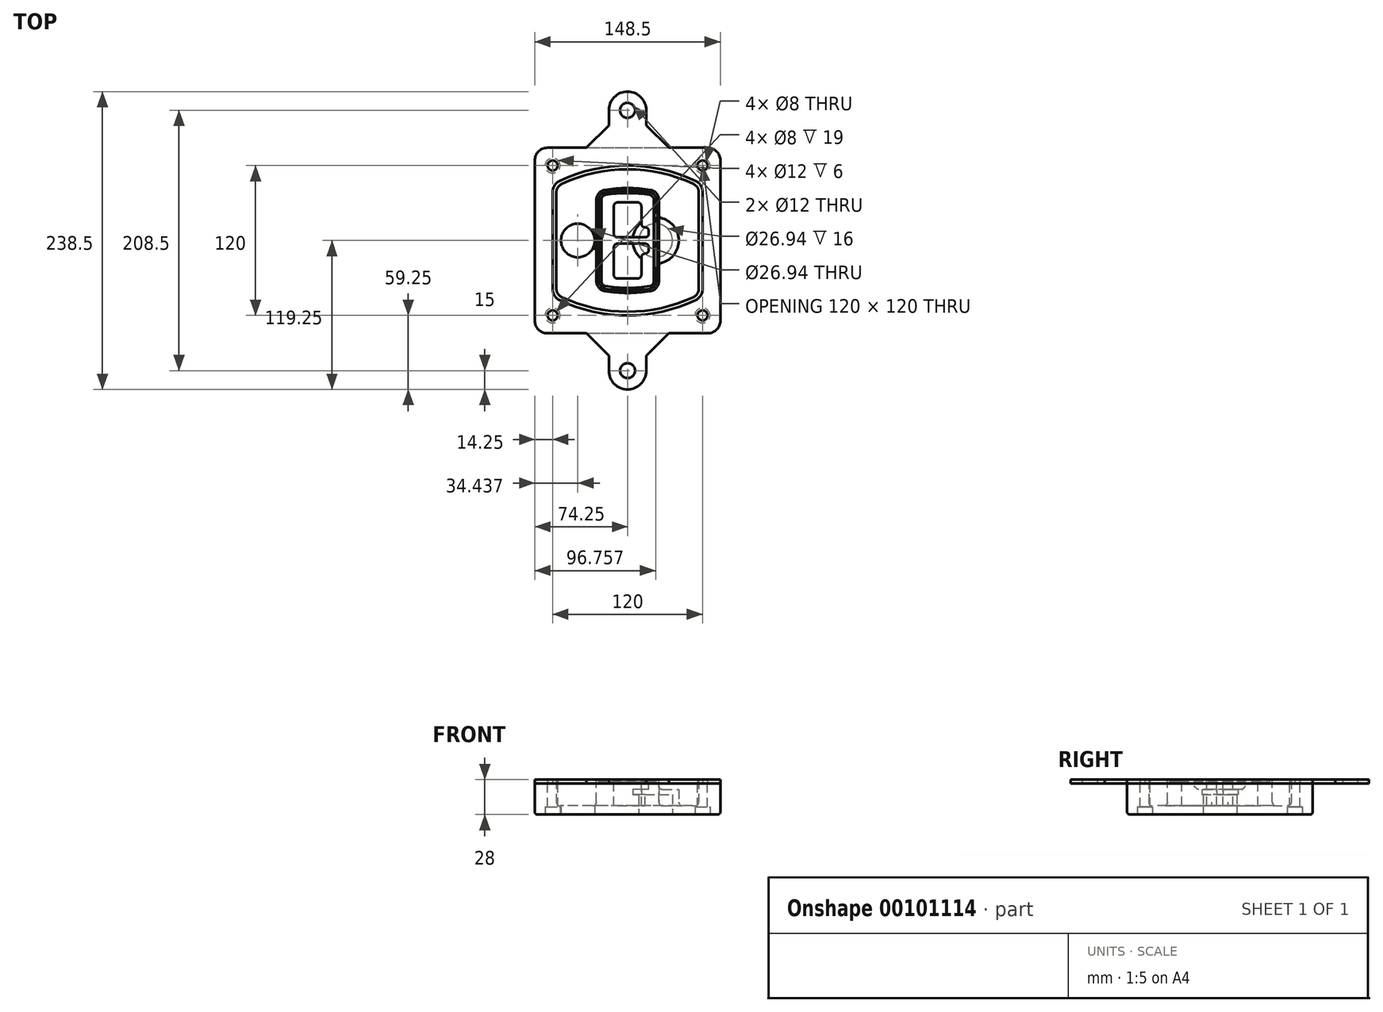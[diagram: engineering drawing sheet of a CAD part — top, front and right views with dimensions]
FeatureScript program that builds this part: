
annotation { "Feature Type Name" : "Feature", "Feature Type Description" : "" }
export const myFeature = defineFeature(function(context is Context, id is Id, definition is map)
    precondition{}
    {
        {
            var Q0;
            Q0=qCreatedBy(makeId("Top.planeOp"),FACE);
            var sketch = newSketch(context, id + "F0", { "sketchPlane" : qUnion([Q0])});
            skPoint(sketch, "E0.rect.middle", {"position": v(0, 0) * mm});
            skLineSegment(sketch, "E1.bottom", {"start": v(-64.25, -74.25) * mm, "end": v(64.25, -74.25) * mm});
            skLineSegment(sketch, "E1.top", {"start": v(-64.25, 74.25) * mm, "end": v(64.25, 74.25) * mm});
            skLineSegment(sketch, "E1.left", {"start": v(-74.25, -64.25) * mm, "end": v(-74.25, 64.25) * mm});
            skLineSegment(sketch, "E1.right", {"start": v(74.25, -64.25) * mm, "end": v(74.25, 64.25) * mm});
            skLineSegment(sketch, "E2", {"start": v(-74.25, 74.25) * mm, "end": v(74.25, -74.25) * mm, "construction": true});
            skLineSegment(sketch, "E3", {"start": v(74.25, 74.25) * mm, "end": v(-74.25, -74.25) * mm, "construction": true});
            skCircle(sketch, "E4", {"center": v(-60, 60) * mm, "radius": 4 * mm});
            skCircle(sketch, "E5", {"center": v(60, 60) * mm, "radius": 4 * mm});
            skCircle(sketch, "E6", {"center": v(60, -60) * mm, "radius": 4 * mm});
            skCircle(sketch, "E7", {"center": v(-60, -60) * mm, "radius": 4 * mm});
            skLineSegment(sketch, "E8", {"start": v(-60, 60) * mm, "end": v(60, 60) * mm, "construction": true});
            skLineSegment(sketch, "E9", {"start": v(60, 60) * mm, "end": v(60, -60) * mm, "construction": true});
            skLineSegment(sketch, "E10", {"start": v(60, -60) * mm, "end": v(-60, -60) * mm, "construction": true});
            skLineSegment(sketch, "E11", {"start": v(-60, -60) * mm, "end": v(-60, 60) * mm, "construction": true});
            skLineSegment(sketch, "E12", {"start": v(-60, 38.83) * mm, "end": v(-60, -38.83) * mm});
            skLineSegment(sketch, "E13", {"start": v(60, 38.83) * mm, "end": v(60, -38.83) * mm});
            skArc(sketch, "E14", {"start": v(54.26, 47.88) * mm, "mid": v(0, 60) * mm, "end": v(-54.26, 47.88) * mm});
            skArc(sketch, "E15", {"start": v(-54.26, -47.88) * mm, "mid": v(0, -60) * mm, "end": v(54.26, -47.88) * mm});
            skLineSegment(sketch, "E16", {"start": v(-60, 0) * mm, "end": v(60, 0) * mm, "construction": true});
            skPoint(sketch, "E17.visualSharp", {"position": v(-60, -45) * mm});
            skArc(sketch, "E17.filletArc", {"start": v(-60, -38.83) * mm, "mid": v(-58.44, -44.2) * mm, "end": v(-54.26, -47.88) * mm});
            skPoint(sketch, "E18.visualSharp", {"position": v(-60, 45) * mm});
            skArc(sketch, "E18.filletArc", {"start": v(-54.26, 47.88) * mm, "mid": v(-58.44, 44.2) * mm, "end": v(-60, 38.83) * mm});
            skPoint(sketch, "E19.visualSharp", {"position": v(60, 45) * mm});
            skArc(sketch, "E19.filletArc", {"start": v(60, 38.83) * mm, "mid": v(58.44, 44.2) * mm, "end": v(54.26, 47.88) * mm});
            skPoint(sketch, "E20.visualSharp", {"position": v(60, -45) * mm});
            skArc(sketch, "E20.filletArc", {"start": v(54.26, -47.88) * mm, "mid": v(58.44, -44.2) * mm, "end": v(60, -38.83) * mm});
            skPoint(sketch, "E21.visualSharp", {"position": v(-74.25, 74.25) * mm});
            skArc(sketch, "E21.filletArc", {"start": v(-64.25, 74.25) * mm, "mid": v(-71.32, 71.32) * mm, "end": v(-74.25, 64.25) * mm});
            skPoint(sketch, "E22.visualSharp", {"position": v(74.25, 74.25) * mm});
            skArc(sketch, "E22.filletArc", {"start": v(74.25, 64.25) * mm, "mid": v(71.32, 71.32) * mm, "end": v(64.25, 74.25) * mm});
            skPoint(sketch, "E23.visualSharp", {"position": v(74.25, -74.25) * mm});
            skArc(sketch, "E23.filletArc", {"start": v(64.25, -74.25) * mm, "mid": v(71.32, -71.32) * mm, "end": v(74.25, -64.25) * mm});
            skPoint(sketch, "E24.visualSharp", {"position": v(-74.25, -74.25) * mm});
            skArc(sketch, "E24.filletArc", {"start": v(-74.25, -64.25) * mm, "mid": v(-71.32, -71.32) * mm, "end": v(-64.25, -74.25) * mm});
            skArc(sketch, "E25.0", {"start": v(57, 38.83) * mm, "mid": v(55.9, 42.58) * mm, "end": v(52.98, 45.17) * mm});
            skLineSegment(sketch, "E25.1", {"start": v(57, 38.83) * mm, "end": v(57, -38.83) * mm});
            skArc(sketch, "E25.2", {"start": v(52.98, -45.17) * mm, "mid": v(55.9, -42.58) * mm, "end": v(57, -38.83) * mm});
            skArc(sketch, "E25.3", {"start": v(-52.98, -45.17) * mm, "mid": v(0, -57) * mm, "end": v(52.98, -45.17) * mm});
            skArc(sketch, "E25.4", {"start": v(-57, -38.83) * mm, "mid": v(-55.9, -42.58) * mm, "end": v(-52.98, -45.17) * mm});
            skArc(sketch, "E25.5", {"start": v(52.98, 45.17) * mm, "mid": v(0, 57) * mm, "end": v(-52.98, 45.17) * mm});
            skLineSegment(sketch, "E25.6", {"start": v(-57, 38.83) * mm, "end": v(-57, -38.83) * mm});
            skArc(sketch, "E25.7", {"start": v(-52.98, 45.17) * mm, "mid": v(-55.9, 42.58) * mm, "end": v(-57, 38.83) * mm});
            skArc(sketch, "E26.0", {"start": v(-55.96, 51.5) * mm, "mid": v(-61.82, 46.33) * mm, "end": v(-64, 38.83) * mm});
            skArc(sketch, "E26.1", {"start": v(55.96, 51.5) * mm, "mid": v(0, 64) * mm, "end": v(-55.96, 51.5) * mm});
            skArc(sketch, "E26.2", {"start": v(64, 38.83) * mm, "mid": v(61.82, 46.33) * mm, "end": v(55.96, 51.5) * mm});
            skLineSegment(sketch, "E26.3", {"start": v(64, 38.83) * mm, "end": v(64, -38.83) * mm});
            skArc(sketch, "E26.4", {"start": v(55.96, -51.5) * mm, "mid": v(61.82, -46.33) * mm, "end": v(64, -38.83) * mm});
            skLineSegment(sketch, "E26.5", {"start": v(-64, 38.83) * mm, "end": v(-64, -38.83) * mm});
            skArc(sketch, "E26.6", {"start": v(-55.96, -51.5) * mm, "mid": v(0, -64) * mm, "end": v(55.96, -51.5) * mm});
            skArc(sketch, "E26.7", {"start": v(-64, -38.83) * mm, "mid": v(-61.82, -46.33) * mm, "end": v(-55.96, -51.5) * mm});
            skSolve(sketch);
        }
        {
            var Q0;
            Q0=makeQuery(id+"F0.imprint","IMPRINT",FACE,{"disambiguationData":[TD([[makeQuery(id+"F0.imprint","IMPRINT",EDGE,{"derivedFrom":sQuery(id+"F0.wireOp",EDGE,"E1.bottom")}),1.0]])]});
            var Q1;
            Q1=makeQuery(id+"F0.imprint","IMPRINT",FACE,{"disambiguationData":[TD([[makeQuery(id+"F0.imprint","IMPRINT",EDGE,{"derivedFrom":sQuery(id+"F0.wireOp",EDGE,"E12")}),1.0]])]});
            var Q2;
            Q2=makeQuery(id+"F0.imprint","IMPRINT",FACE,{"disambiguationData":[TD([[makeQuery(id+"F0.imprint","IMPRINT",EDGE,{"derivedFrom":sQuery(id+"F0.wireOp",EDGE,"E25.0")}),1.0]])]});
            var Q3;
            Q3=makeQuery(id+"F0.imprint","IMPRINT",FACE,{"disambiguationData":[TD([[makeQuery(id+"F0.imprint","IMPRINT",EDGE,{"derivedFrom":sQuery(id+"F0.wireOp",EDGE,"E12")}),-1.0]])]});
            extrude(context, id + "F1", {"entities" : qUnion([Q0, Q1, Q2, Q3]), "oppositeDirection" : true, "depth" : 25 * mm});
        }
        {
            var Q0;
            Q0=makeQuery(id+"F0.imprint","IMPRINT",FACE,{"disambiguationData":[TD([[makeQuery(id+"F0.imprint","IMPRINT",EDGE,{"derivedFrom":sQuery(id+"F0.wireOp",EDGE,"E12")}),1.0]])]});
            extrude(context, id + "F2", {"entities" : qUnion([Q0]), "operationType" : NewBodyOperationType.ADD, "depth" : 3 * mm});
        }
        {
            var Q0;
            Q0=makeQuery(id+"F0.imprint","IMPRINT",FACE,{"disambiguationData":[TD([[makeQuery(id+"F0.imprint","IMPRINT",EDGE,{"derivedFrom":sQuery(id+"F0.wireOp",EDGE,"E25.0")}),1.0]])]});
            extrude(context, id + "F3", {"entities" : qUnion([Q0]), "operationType" : NewBodyOperationType.REMOVE, "oppositeDirection" : true, "depth" : 18 * mm});
        }
        {
            var Q0;
            Q0=makeQuery(id+"F2.opExtrude","CAP_FACE",FACE,{"disambiguationData":[OSD([sQuery(id+"F0.wireOp",EDGE,"E12"),sQuery(id+"F0.wireOp",EDGE,"E13"),sQuery(id+"F0.wireOp",EDGE,"E14"),sQuery(id+"F0.wireOp",EDGE,"E15"),sQuery(id+"F0.wireOp",EDGE,"E17.filletArc"),sQuery(id+"F0.wireOp",EDGE,"E18.filletArc"),sQuery(id+"F0.wireOp",EDGE,"E19.filletArc"),sQuery(id+"F0.wireOp",EDGE,"E20.filletArc"),sQuery(id+"F0.wireOp",EDGE,"E25.0"),sQuery(id+"F0.wireOp",EDGE,"E25.1"),sQuery(id+"F0.wireOp",EDGE,"E25.2"),sQuery(id+"F0.wireOp",EDGE,"E25.3"),sQuery(id+"F0.wireOp",EDGE,"E25.4"),sQuery(id+"F0.wireOp",EDGE,"E25.5"),sQuery(id+"F0.wireOp",EDGE,"E25.6"),sQuery(id+"F0.wireOp",EDGE,"E25.7")])],"isStart":false});
            var sketch = newSketch(context, id + "F4", { "sketchPlane" : qUnion([Q0])});
            skArc(sketch, "E27.0", {"start": v(-18.34, -40.45) * mm, "mid": v(0, -42) * mm, "end": v(18.34, -40.45) * mm});
            skArc(sketch, "E28.0", {"start": v(18.34, 40.45) * mm, "mid": v(0, 42) * mm, "end": v(-18.34, 40.45) * mm});
            skLineSegment(sketch, "E29", {"start": v(-25, 32.57) * mm, "end": v(-25, -32.57) * mm});
            skLineSegment(sketch, "E30", {"start": v(25, 32.57) * mm, "end": v(25, -32.57) * mm});
            skLineSegment(sketch, "E31", {"start": v(-25, 39.1) * mm, "end": v(25, 39.1) * mm, "construction": true});
            skLineSegment(sketch, "E32", {"start": v(-25, -39.1) * mm, "end": v(25, -39.1) * mm, "construction": true});
            skPoint(sketch, "E33.visualSharp", {"position": v(-25, 39.1) * mm});
            skArc(sketch, "E33.filletArc", {"start": v(-18.34, 40.45) * mm, "mid": v(-23.11, 37.73) * mm, "end": v(-25, 32.57) * mm});
            skPoint(sketch, "E34.visualSharp", {"position": v(25, 39.1) * mm});
            skArc(sketch, "E34.filletArc", {"start": v(25, 32.57) * mm, "mid": v(23.11, 37.73) * mm, "end": v(18.34, 40.45) * mm});
            skPoint(sketch, "E35.visualSharp", {"position": v(25, -39.1) * mm});
            skArc(sketch, "E35.filletArc", {"start": v(18.34, -40.45) * mm, "mid": v(23.11, -37.73) * mm, "end": v(25, -32.57) * mm});
            skPoint(sketch, "E36.visualSharp", {"position": v(-25, -39.1) * mm});
            skArc(sketch, "E36.filletArc", {"start": v(-25, -32.57) * mm, "mid": v(-23.11, -37.73) * mm, "end": v(-18.34, -40.45) * mm});
            skArc(sketch, "E37.0", {"start": v(52.98, 45.17) * mm, "mid": v(0, 57) * mm, "end": v(-52.98, 45.17) * mm});
            skArc(sketch, "E37.1", {"start": v(-52.98, 45.17) * mm, "mid": v(-55.9, 42.58) * mm, "end": v(-57, 38.83) * mm});
            skLineSegment(sketch, "E37.2", {"start": v(-57, 38.83) * mm, "end": v(-57, -38.83) * mm});
            skArc(sketch, "E37.3", {"start": v(-57, -38.83) * mm, "mid": v(-55.9, -42.58) * mm, "end": v(-52.98, -45.17) * mm});
            skArc(sketch, "E37.4", {"start": v(-52.98, -45.17) * mm, "mid": v(0, -57) * mm, "end": v(52.98, -45.17) * mm});
            skArc(sketch, "E37.5", {"start": v(52.98, -45.17) * mm, "mid": v(55.9, -42.58) * mm, "end": v(57, -38.83) * mm});
            skLineSegment(sketch, "E37.6", {"start": v(57, 38.83) * mm, "end": v(57, -38.83) * mm});
            skArc(sketch, "E37.7", {"start": v(57, 38.83) * mm, "mid": v(55.9, 42.58) * mm, "end": v(52.98, 45.17) * mm});
            skLineSegment(sketch, "E38.0", {"start": v(23, 32.57) * mm, "end": v(23, -32.57) * mm});
            skArc(sketch, "E38.1", {"start": v(18, -38.48) * mm, "mid": v(21.58, -36.44) * mm, "end": v(23, -32.57) * mm});
            skArc(sketch, "E38.2", {"start": v(-18, -38.48) * mm, "mid": v(0, -40) * mm, "end": v(18, -38.48) * mm});
            skArc(sketch, "E38.3", {"start": v(-23, -32.57) * mm, "mid": v(-21.58, -36.44) * mm, "end": v(-18, -38.48) * mm});
            skLineSegment(sketch, "E38.4", {"start": v(-23, 32.57) * mm, "end": v(-23, -32.57) * mm});
            skArc(sketch, "E38.5", {"start": v(23, 32.57) * mm, "mid": v(21.58, 36.44) * mm, "end": v(18, 38.48) * mm});
            skArc(sketch, "E38.6", {"start": v(-18, 38.48) * mm, "mid": v(-21.58, 36.44) * mm, "end": v(-23, 32.57) * mm});
            skArc(sketch, "E38.7", {"start": v(18, 38.48) * mm, "mid": v(0, 40) * mm, "end": v(-18, 38.48) * mm});
            skArc(sketch, "E39.0", {"start": v(21, 32.57) * mm, "mid": v(20.06, 35.15) * mm, "end": v(17.67, 36.5) * mm});
            skLineSegment(sketch, "E39.1", {"start": v(21, 32.57) * mm, "end": v(21, -32.57) * mm});
            skArc(sketch, "E39.2", {"start": v(17.67, -36.5) * mm, "mid": v(20.06, -35.15) * mm, "end": v(21, -32.57) * mm});
            skArc(sketch, "E39.3", {"start": v(-17.67, -36.5) * mm, "mid": v(0, -38) * mm, "end": v(17.67, -36.5) * mm});
            skArc(sketch, "E39.4", {"start": v(-21, -32.57) * mm, "mid": v(-20.06, -35.15) * mm, "end": v(-17.67, -36.5) * mm});
            skArc(sketch, "E39.5", {"start": v(17.67, 36.5) * mm, "mid": v(0, 38) * mm, "end": v(-17.67, 36.5) * mm});
            skLineSegment(sketch, "E39.6", {"start": v(-21, 32.57) * mm, "end": v(-21, -32.57) * mm});
            skArc(sketch, "E39.7", {"start": v(-17.67, 36.5) * mm, "mid": v(-20.06, 35.15) * mm, "end": v(-21, 32.57) * mm});
            skLineSegment(sketch, "E40", {"start": v(-25, 0) * mm, "end": v(25, 0) * mm, "construction": true});
            skLineSegment(sketch, "E41", {"start": v(-11, 5.5) * mm, "end": v(-11, 27.5) * mm});
            skLineSegment(sketch, "E42", {"start": v(-8, 30.5) * mm, "end": v(8, 30.5) * mm});
            skLineSegment(sketch, "E43", {"start": v(11, 27.5) * mm, "end": v(11, 13.5) * mm});
            skLineSegment(sketch, "E44", {"start": v(14, 10.5) * mm, "end": v(14, 10.5) * mm});
            skLineSegment(sketch, "E45", {"start": v(17, 7.5) * mm, "end": v(17, 5.5) * mm});
            skLineSegment(sketch, "E46", {"start": v(14, 2.5) * mm, "end": v(-8, 2.5) * mm});
            skPoint(sketch, "E47.visualSharp", {"position": v(-11, 30.5) * mm});
            skArc(sketch, "E47.filletArc", {"start": v(-8, 30.5) * mm, "mid": v(-10.12, 29.62) * mm, "end": v(-11, 27.5) * mm});
            skPoint(sketch, "E48.visualSharp", {"position": v(11, 30.5) * mm});
            skArc(sketch, "E48.filletArc", {"start": v(11, 27.5) * mm, "mid": v(10.12, 29.62) * mm, "end": v(8, 30.5) * mm});
            skPoint(sketch, "E49.visualSharp", {"position": v(11, 10.5) * mm});
            skArc(sketch, "E49.filletArc", {"start": v(11, 13.5) * mm, "mid": v(11.88, 11.38) * mm, "end": v(14, 10.5) * mm});
            skPoint(sketch, "E50.visualSharp", {"position": v(17, 10.5) * mm});
            skArc(sketch, "E50.filletArc", {"start": v(17, 7.5) * mm, "mid": v(16.12, 9.62) * mm, "end": v(14, 10.5) * mm});
            skPoint(sketch, "E51.visualSharp", {"position": v(17, 2.5) * mm});
            skArc(sketch, "E51.filletArc", {"start": v(14, 2.5) * mm, "mid": v(16.12, 3.38) * mm, "end": v(17, 5.5) * mm});
            skPoint(sketch, "E52.visualSharp", {"position": v(-11, 2.5) * mm});
            skArc(sketch, "E52.filletArc", {"start": v(-11, 5.5) * mm, "mid": v(-10.12, 3.38) * mm, "end": v(-8, 2.5) * mm});
            skLineSegment(sketch, "E53.0.MirrorCS", {"start": v(14, -2.5) * mm, "end": v(-8, -2.5) * mm});
            skArc(sketch, "E54.0.MirrorCS", {"start": v(-11, -5.5) * mm, "mid": v(-10.12, -3.38) * mm, "end": v(-8, -2.5) * mm});
            skLineSegment(sketch, "E55.0.MirrorCS", {"start": v(-11, -5.5) * mm, "end": v(-11, -27.5) * mm});
            skArc(sketch, "E56.0.MirrorCS", {"start": v(-8, -30.5) * mm, "mid": v(-10.12, -29.62) * mm, "end": v(-11, -27.5) * mm});
            skLineSegment(sketch, "E57.0.MirrorCS", {"start": v(-8, -30.5) * mm, "end": v(8, -30.5) * mm});
            skArc(sketch, "E58.0.MirrorCS", {"start": v(11, -27.5) * mm, "mid": v(10.12, -29.62) * mm, "end": v(8, -30.5) * mm});
            skLineSegment(sketch, "E59.0.MirrorCS", {"start": v(11, -27.5) * mm, "end": v(11, -13.5) * mm});
            skArc(sketch, "E60.0.MirrorCS", {"start": v(11, -13.5) * mm, "mid": v(11.88, -11.38) * mm, "end": v(14, -10.5) * mm});
            skArc(sketch, "E61.0.MirrorCS", {"start": v(17, -7.5) * mm, "mid": v(16.12, -9.62) * mm, "end": v(14, -10.5) * mm});
            skLineSegment(sketch, "E62.0.MirrorCS", {"start": v(17, -7.5) * mm, "end": v(17, -5.5) * mm});
            skArc(sketch, "E63.0.MirrorCS", {"start": v(14, -2.5) * mm, "mid": v(16.12, -3.38) * mm, "end": v(17, -5.5) * mm});
            skSolve(sketch);
        }
        {
            var Q0;
            Q0=makeQuery(id+"F4.imprint","IMPRINT",FACE,{"disambiguationData":[TD([[makeQuery(id+"F4.imprint","IMPRINT",EDGE,{"derivedFrom":sQuery(id+"F4.wireOp",EDGE,"E27.0")}),1.0]])]});
            var Q1;
            Q1=makeQuery(id+"F4.imprint","IMPRINT",FACE,{"disambiguationData":[TD([[makeQuery(id+"F4.imprint","IMPRINT",EDGE,{"derivedFrom":sQuery(id+"F4.wireOp",EDGE,"E38.0")}),-1.0]])]});
            var Q2;
            Q2=makeQuery(id+"F4.imprint","IMPRINT",FACE,{"disambiguationData":[TD([[makeQuery(id+"F4.imprint","IMPRINT",EDGE,{"derivedFrom":sQuery(id+"F4.wireOp",EDGE,"E39.0")}),1.0]])]});
            extrude(context, id + "F5", {"entities" : qUnion([Q0, Q1, Q2]), "operationType" : NewBodyOperationType.ADD, "endBound" : BoundingType.UP_TO_NEXT, "oppositeDirection" : true, "depth" : 25 * mm});
        }
        {
            var Q0;
            Q0=makeQuery(id+"F4.imprint","IMPRINT",FACE,{"disambiguationData":[TD([[makeQuery(id+"F4.imprint","IMPRINT",EDGE,{"derivedFrom":sQuery(id+"F4.wireOp",EDGE,"E38.0")}),-1.0]])]});
            extrude(context, id + "F6", {"entities" : qUnion([Q0]), "operationType" : NewBodyOperationType.REMOVE, "oppositeDirection" : true, "depth" : 2 * mm});
        }
        {
            var Q0;
            Q0=makeQuery(id+"F1.opExtrude","CAP_FACE",FACE,{"disambiguationData":[OSD([sQuery(id+"F0.wireOp",EDGE,"E1.bottom"),sQuery(id+"F0.wireOp",EDGE,"E1.top"),sQuery(id+"F0.wireOp",EDGE,"E1.left"),sQuery(id+"F0.wireOp",EDGE,"E1.right"),sQuery(id+"F0.wireOp",EDGE,"E4"),sQuery(id+"F0.wireOp",EDGE,"E5"),sQuery(id+"F0.wireOp",EDGE,"E6"),sQuery(id+"F0.wireOp",EDGE,"E7"),sQuery(id+"F0.wireOp",EDGE,"E21.filletArc"),sQuery(id+"F0.wireOp",EDGE,"E22.filletArc"),sQuery(id+"F0.wireOp",EDGE,"E23.filletArc"),sQuery(id+"F0.wireOp",EDGE,"E24.filletArc")])],"isStart":false});
            var sketch = newSketch(context, id + "F7", { "sketchPlane" : qUnion([Q0])});
            skCircle(sketch, "E64", {"center": v(22.5, 0) * mm, "radius": 13.47 * mm});
            skCircle(sketch, "E65", {"center": v(-39.81, 0) * mm, "radius": 13.47 * mm});
            skLineSegment(sketch, "E66", {"start": v(74.25, 0) * mm, "end": v(-74.25, 0) * mm});
            skCircle(sketch, "E67", {"center": v(22.5, 0) * mm, "radius": 18.47 * mm});
            skCircle(sketch, "E68", {"center": v(60, -60) * mm, "radius": 6 * mm});
            skCircle(sketch, "E69", {"center": v(-60, -60) * mm, "radius": 6 * mm});
            skCircle(sketch, "E70", {"center": v(-60, 60) * mm, "radius": 6 * mm});
            skCircle(sketch, "E71", {"center": v(60, 60) * mm, "radius": 6 * mm});
            skSolve(sketch);
        }
        {
            var Q0;
            {var subQ1=sQuery(id+"F7.wireOp",EDGE,"E66");var subQ4=sQuery(id+"F7.wireOp",EDGE,"E64");var subQ6=makeQuery(id+"F7.imprint","INTERSECT",VERTEX,{"disambiguationData":[OD(0.0)],"derivedFrom":[subQ4,subQ1]});Q0=makeQuery(id+"F7.imprint","IMPRINT",FACE,{"disambiguationData":[TD([[makeQuery(id+"F7.imprint","IMPRINT",EDGE,{"disambiguationData":[TD([[subQ6,-1.0]])],"derivedFrom":subQ4}),-1.0]])]});}
            var Q1;
            {var subQ0=sQuery(id+"F7.wireOp",EDGE,"E66");var subQ1=sQuery(id+"F7.wireOp",EDGE,"E64");var subQ3=makeQuery(id+"F7.imprint","INTERSECT",VERTEX,{"disambiguationData":[OD(0.0)],"derivedFrom":[subQ1,subQ0]});Q1=makeQuery(id+"F7.imprint","IMPRINT",FACE,{"disambiguationData":[TD([[makeQuery(id+"F7.imprint","IMPRINT",EDGE,{"disambiguationData":[TD([[subQ3,-1.0]])],"derivedFrom":subQ1}),1.0]])]});}
            var Q2;
            {var subQ0=sQuery(id+"F7.wireOp",EDGE,"E66");var subQ1=sQuery(id+"F7.wireOp",EDGE,"E64");var subQ3=makeQuery(id+"F7.imprint","INTERSECT",VERTEX,{"disambiguationData":[OD(0.0)],"derivedFrom":[subQ1,subQ0]});Q2=makeQuery(id+"F7.imprint","IMPRINT",FACE,{"disambiguationData":[TD([[makeQuery(id+"F7.imprint","IMPRINT",EDGE,{"disambiguationData":[TD([[subQ3,1.0]])],"derivedFrom":subQ1}),1.0]])]});}
            var Q3;
            {var subQ1=sQuery(id+"F7.wireOp",EDGE,"E66");var subQ4=sQuery(id+"F7.wireOp",EDGE,"E64");var subQ6=makeQuery(id+"F7.imprint","INTERSECT",VERTEX,{"disambiguationData":[OD(0.0)],"derivedFrom":[subQ4,subQ1]});Q3=makeQuery(id+"F7.imprint","IMPRINT",FACE,{"disambiguationData":[TD([[makeQuery(id+"F7.imprint","IMPRINT",EDGE,{"disambiguationData":[TD([[subQ6,1.0]])],"derivedFrom":subQ4}),-1.0]])]});}
            extrude(context, id + "F8", {"entities" : qUnion([Q0, Q1, Q2, Q3]), "operationType" : NewBodyOperationType.ADD, "oppositeDirection" : true, "depth" : 20 * mm});
        }
        {
            var Q0;
            {var subQ0=sQuery(id+"F7.wireOp",EDGE,"E66");var subQ1=sQuery(id+"F7.wireOp",EDGE,"E64");var subQ3=makeQuery(id+"F7.imprint","INTERSECT",VERTEX,{"disambiguationData":[OD(0.0)],"derivedFrom":[subQ1,subQ0]});Q0=makeQuery(id+"F7.imprint","IMPRINT",FACE,{"disambiguationData":[TD([[makeQuery(id+"F7.imprint","IMPRINT",EDGE,{"disambiguationData":[TD([[subQ3,-1.0]])],"derivedFrom":subQ1}),1.0]])]});}
            var Q1;
            {var subQ0=sQuery(id+"F7.wireOp",EDGE,"E66");var subQ1=sQuery(id+"F7.wireOp",EDGE,"E64");var subQ3=makeQuery(id+"F7.imprint","INTERSECT",VERTEX,{"disambiguationData":[OD(0.0)],"derivedFrom":[subQ1,subQ0]});Q1=makeQuery(id+"F7.imprint","IMPRINT",FACE,{"disambiguationData":[TD([[makeQuery(id+"F7.imprint","IMPRINT",EDGE,{"disambiguationData":[TD([[subQ3,1.0]])],"derivedFrom":subQ1}),1.0]])]});}
            extrude(context, id + "F9", {"entities" : qUnion([Q0, Q1]), "operationType" : NewBodyOperationType.REMOVE, "oppositeDirection" : true, "depth" : 16 * mm});
        }
        {
            var Q0;
            {var subQ0=sQuery(id+"F7.wireOp",EDGE,"E66");var subQ1=sQuery(id+"F7.wireOp",EDGE,"E65");var subQ3=makeQuery(id+"F7.imprint","INTERSECT",VERTEX,{"disambiguationData":[OD(0.0)],"derivedFrom":[subQ1,subQ0]});Q0=makeQuery(id+"F7.imprint","IMPRINT",FACE,{"disambiguationData":[TD([[makeQuery(id+"F7.imprint","IMPRINT",EDGE,{"disambiguationData":[TD([[subQ3,-1.0]])],"derivedFrom":subQ1}),1.0]])]});}
            var Q1;
            {var subQ0=sQuery(id+"F7.wireOp",EDGE,"E66");var subQ1=sQuery(id+"F7.wireOp",EDGE,"E65");var subQ3=makeQuery(id+"F7.imprint","INTERSECT",VERTEX,{"disambiguationData":[OD(0.0)],"derivedFrom":[subQ1,subQ0]});Q1=makeQuery(id+"F7.imprint","IMPRINT",FACE,{"disambiguationData":[TD([[makeQuery(id+"F7.imprint","IMPRINT",EDGE,{"disambiguationData":[TD([[subQ3,1.0]])],"derivedFrom":subQ1}),1.0]])]});}
            extrude(context, id + "F10", {"entities" : qUnion([Q0, Q1]), "operationType" : NewBodyOperationType.REMOVE, "oppositeDirection" : true, "depth" : 25 * mm});
        }
        {
            var Q0;
            Q0=makeQuery(id+"F7.imprint","IMPRINT",FACE,{"disambiguationData":[TD([[makeQuery(id+"F7.imprint","IMPRINT",EDGE,{"derivedFrom":sQuery(id+"F7.wireOp",EDGE,"E68")}),1.0]])]});
            var Q1;
            Q1=makeQuery(id+"F7.imprint","IMPRINT",FACE,{"disambiguationData":[TD([[makeQuery(id+"F7.imprint","IMPRINT",EDGE,{"derivedFrom":makeQuery(id+"F1.opExtrude","CAP_EDGE",EDGE,{"disambiguationData":[OSD([sQuery(id+"F0.wireOp",EDGE,"E5")])],"isStart":false})}),-1.0]])]});
            var Q2;
            Q2=makeQuery(id+"F7.imprint","IMPRINT",FACE,{"disambiguationData":[TD([[makeQuery(id+"F7.imprint","IMPRINT",EDGE,{"derivedFrom":sQuery(id+"F7.wireOp",EDGE,"E69")}),1.0]])]});
            var Q3;
            Q3=makeQuery(id+"F7.imprint","IMPRINT",FACE,{"disambiguationData":[TD([[makeQuery(id+"F7.imprint","IMPRINT",EDGE,{"derivedFrom":makeQuery(id+"F1.opExtrude","CAP_EDGE",EDGE,{"disambiguationData":[OSD([sQuery(id+"F0.wireOp",EDGE,"E4")])],"isStart":false})}),-1.0]])]});
            var Q4;
            Q4=makeQuery(id+"F7.imprint","IMPRINT",FACE,{"disambiguationData":[TD([[makeQuery(id+"F7.imprint","IMPRINT",EDGE,{"derivedFrom":sQuery(id+"F7.wireOp",EDGE,"E70")}),1.0]])]});
            var Q5;
            Q5=makeQuery(id+"F7.imprint","IMPRINT",FACE,{"disambiguationData":[TD([[makeQuery(id+"F7.imprint","IMPRINT",EDGE,{"derivedFrom":makeQuery(id+"F1.opExtrude","CAP_EDGE",EDGE,{"disambiguationData":[OSD([sQuery(id+"F0.wireOp",EDGE,"E7")])],"isStart":false})}),-1.0]])]});
            var Q6;
            Q6=makeQuery(id+"F7.imprint","IMPRINT",FACE,{"disambiguationData":[TD([[makeQuery(id+"F7.imprint","IMPRINT",EDGE,{"derivedFrom":sQuery(id+"F7.wireOp",EDGE,"E71")}),1.0]])]});
            var Q7;
            Q7=makeQuery(id+"F7.imprint","IMPRINT",FACE,{"disambiguationData":[TD([[makeQuery(id+"F7.imprint","IMPRINT",EDGE,{"derivedFrom":makeQuery(id+"F1.opExtrude","CAP_EDGE",EDGE,{"disambiguationData":[OSD([sQuery(id+"F0.wireOp",EDGE,"E6")])],"isStart":false})}),-1.0]])]});
            extrude(context, id + "F11", {"entities" : qUnion([Q0, Q1, Q2, Q3, Q4, Q5, Q6, Q7]), "operationType" : NewBodyOperationType.REMOVE, "oppositeDirection" : true, "depth" : 6 * mm});
        }
        {
            var Q0;
            Q0=makeQuery(id+"F9.boolean.opBoolean","COPY",FACE,{"derivedFrom":makeQuery(id+"F9.opExtrude","CAP_FACE",FACE,{"disambiguationData":[OSD([sQuery(id+"F7.wireOp",EDGE,"E64")])],"isStart":false})});
            var sketch = newSketch(context, id + "F12", { "sketchPlane" : qUnion([Q0])});
            skArc(sketch, "E72.0", {"start": v(11, 14.45) * mm, "mid": v(6.45, 9.13) * mm, "end": v(4.2, 2.5) * mm});
            skArc(sketch, "E72.1", {"start": v(4.2, -2.5) * mm, "mid": v(6.45, -9.13) * mm, "end": v(11, -14.45) * mm});
            skLineSegment(sketch, "E73", {"start": v(4.2, -2.5) * mm, "end": v(14, -2.5) * mm});
            skLineSegment(sketch, "E74.0", {"start": v(14, 2.5) * mm, "end": v(4.2, 2.5) * mm});
            skArc(sketch, "E74.1", {"start": v(14, 2.5) * mm, "mid": v(16.12, 3.38) * mm, "end": v(17, 5.5) * mm});
            skLineSegment(sketch, "E74.2", {"start": v(17, 7.5) * mm, "end": v(17, 5.5) * mm});
            skArc(sketch, "E74.3", {"start": v(17, 7.5) * mm, "mid": v(16.12, 9.62) * mm, "end": v(14, 10.5) * mm});
            skArc(sketch, "E74.4", {"start": v(11, 13.5) * mm, "mid": v(11.88, 11.38) * mm, "end": v(14, 10.5) * mm});
            skLineSegment(sketch, "E74.5", {"start": v(11, 14.45) * mm, "end": v(11, 13.5) * mm});
            skLineSegment(sketch, "E74.7", {"start": v(14, -2.5) * mm, "end": v(4.2, -2.5) * mm});
            skArc(sketch, "E74.8", {"start": v(14, -2.5) * mm, "mid": v(16.12, -3.38) * mm, "end": v(17, -5.5) * mm});
            skLineSegment(sketch, "E74.9", {"start": v(17, -7.5) * mm, "end": v(17, -5.5) * mm});
            skArc(sketch, "E74.10", {"start": v(17, -7.5) * mm, "mid": v(16.12, -9.62) * mm, "end": v(14, -10.5) * mm});
            skArc(sketch, "E74.11", {"start": v(11, -13.5) * mm, "mid": v(11.88, -11.38) * mm, "end": v(14, -10.5) * mm});
            skLineSegment(sketch, "E74.12", {"start": v(11, -14.45) * mm, "end": v(11, -13.5) * mm});
            skPoint(sketch, "E75.orphan", {"position": v(11, -27.5) * mm});
            skPoint(sketch, "E76.orphan", {"position": v(-8, -2.5) * mm});
            skPoint(sketch, "E77.orphan", {"position": v(-8, 2.5) * mm});
            skPoint(sketch, "E78.orphan", {"position": v(11, 27.5) * mm});
            skSolve(sketch);
        }
        {
            var Q0;
            {var subQ7=sQuery(id+"F12.wireOp",EDGE,"E72.0");var subQ14=sQuery(id+"F12.wireOp",EDGE,"E72.1");var subQ16=sQuery(id+"F12.wireOp",EDGE,"E74.1");var subQ18=sQuery(id+"F12.wireOp",EDGE,"E74.8");Q0=qUnion([makeQuery(id+"F12.imprint","IMPRINT",FACE,{"disambiguationData":[TD([[makeQuery(id+"F12.imprint","IMPRINT",EDGE,{"derivedFrom":subQ7}),1.0]])]}),makeQuery(id+"F12.imprint","IMPRINT",FACE,{"disambiguationData":[TD([[makeQuery(id+"F12.imprint","IMPRINT",EDGE,{"derivedFrom":subQ14}),1.0]])]}),makeQuery(id+"F12.imprint","IMPRINT",FACE,{"disambiguationData":[TD([[makeQuery(id+"F12.imprint","IMPRINT",EDGE,{"derivedFrom":subQ16}),1.0]])]}),makeQuery(id+"F12.imprint","IMPRINT",FACE,{"disambiguationData":[TD([[makeQuery(id+"F12.imprint","IMPRINT",EDGE,{"derivedFrom":subQ18}),-1.0]])]})]);}
            var Q1;
            Q1=makeQuery(id+"F5.boolean.opBoolean","SPLIT",FACE,{"disambiguationData":[TD([makeQuery(id+"F5.opExtrude","SWEPT_FACE",FACE,{"disambiguationData":[OSD([sQuery(id+"F4.wireOp",EDGE,"E41")])]})])],"derivedFrom":makeQuery(id+"F3.boolean.opBoolean","COPY",FACE,{"derivedFrom":makeQuery(id+"F3.opExtrude","CAP_FACE",FACE,{"disambiguationData":[OSD([sQuery(id+"F0.wireOp",EDGE,"E25.0"),sQuery(id+"F0.wireOp",EDGE,"E25.1"),sQuery(id+"F0.wireOp",EDGE,"E25.2"),sQuery(id+"F0.wireOp",EDGE,"E25.3"),sQuery(id+"F0.wireOp",EDGE,"E25.4"),sQuery(id+"F0.wireOp",EDGE,"E25.5"),sQuery(id+"F0.wireOp",EDGE,"E25.6"),sQuery(id+"F0.wireOp",EDGE,"E25.7")])],"isStart":false})})});
            extrude(context, id + "F13", {"entities" : qUnion([Q0]), "operationType" : NewBodyOperationType.REMOVE, "endBound" : BoundingType.UP_TO_SURFACE, "endBoundEntityFace" : qUnion([Q1]), "depth" : 25 * mm});
        }
        {
            var Q0;
            Q0=makeQuery(id+"F3.boolean.opBoolean","COPY",EDGE,{"derivedFrom":makeQuery(id+"F3.opExtrude","CAP_EDGE",EDGE,{"disambiguationData":[OSD([sQuery(id+"F0.wireOp",EDGE,"E25.6")])],"isStart":false})});
            var Q1;
            Q1=makeQuery(id+"F8.boolean.opBoolean","INTERSECT",EDGE,{"derivedFrom":[makeQuery(id+"F5.opExtrude","SWEPT_FACE",FACE,{"disambiguationData":[OSD([sQuery(id+"F4.wireOp",EDGE,"E30")])]}),makeQuery(id+"F8.opExtrude","CAP_FACE",FACE,{"disambiguationData":[OSD([sQuery(id+"F7.wireOp",EDGE,"E67")])],"isStart":false})]});
            var Q2;
            Q2=makeQuery(id+"F8.boolean.opBoolean","INTERSECT",EDGE,{"disambiguationData":[OD(1.0)],"derivedFrom":[makeQuery(id+"F5.opExtrude","SWEPT_FACE",FACE,{"disambiguationData":[OSD([sQuery(id+"F4.wireOp",EDGE,"E30")])]}),makeQuery(id+"F8.opExtrude","SWEPT_FACE",FACE,{"disambiguationData":[OSD([sQuery(id+"F7.wireOp",EDGE,"E67")])]})]});
            var Q3;
            {var subQ0=sQuery(id+"F4.wireOp",EDGE,"E30");Q3=makeQuery(id+"F8.boolean.opBoolean","SPLIT",EDGE,{"disambiguationData":[TD([makeQuery(id+"F5.opExtrude","SWEPT_FACE",FACE,{"disambiguationData":[OSD([sQuery(id+"F4.wireOp",EDGE,"E35.filletArc")])]})])],"derivedFrom":makeQuery(id+"F5.opExtrude","CAP_EDGE",EDGE,{"disambiguationData":[OSD([subQ0])],"isStart":false})});}
            var Q4;
            {var subQ0=sQuery(id+"F0.wireOp",EDGE,"E25.7");var subQ1=sQuery(id+"F0.wireOp",EDGE,"E25.1");var subQ2=sQuery(id+"F0.wireOp",EDGE,"E25.6");var subQ3=sQuery(id+"F0.wireOp",EDGE,"E25.5");var subQ4=sQuery(id+"F0.wireOp",EDGE,"E25.4");var subQ5=sQuery(id+"F0.wireOp",EDGE,"E25.0");var subQ6=sQuery(id+"F0.wireOp",EDGE,"E25.2");var subQ7=sQuery(id+"F0.wireOp",EDGE,"E25.3");Q4=makeQuery(id+"F8.boolean.opBoolean","INTERSECT",EDGE,{"derivedFrom":[makeQuery(id+"F5.boolean.opBoolean","SPLIT",FACE,{"disambiguationData":[TD([makeQuery(id+"F2.opExtrude","SWEPT_FACE",FACE,{"disambiguationData":[OSD([subQ5])]})])],"derivedFrom":makeQuery(id+"F3.boolean.opBoolean","COPY",FACE,{"derivedFrom":makeQuery(id+"F3.opExtrude","CAP_FACE",FACE,{"disambiguationData":[OSD([subQ5,subQ1,subQ6,subQ7,subQ4,subQ3,subQ2,subQ0])],"isStart":false})})}),makeQuery(id+"F8.opExtrude","SWEPT_FACE",FACE,{"disambiguationData":[OSD([sQuery(id+"F7.wireOp",EDGE,"E67")])]})]});}
            var Q5;
            Q5=makeQuery(id+"F8.boolean.opBoolean","INTERSECT",EDGE,{"disambiguationData":[OD(0.0)],"derivedFrom":[makeQuery(id+"F5.opExtrude","SWEPT_FACE",FACE,{"disambiguationData":[OSD([sQuery(id+"F4.wireOp",EDGE,"E30")])]}),makeQuery(id+"F8.opExtrude","SWEPT_FACE",FACE,{"disambiguationData":[OSD([sQuery(id+"F7.wireOp",EDGE,"E67")])]})]});
            fillet(context, id + "F14", {"entities" : qUnion([Q0, Q1, Q2, Q3, Q4, Q5]), "radius" : 3 * mm, "tangentPropagation" : true, "allowEdgeOverflow" : false});
        }
        {
            var Q0;
            Q0=makeQuery(id+"F1.opExtrude","CAP_EDGE",EDGE,{"disambiguationData":[OSD([sQuery(id+"F0.wireOp",EDGE,"E1.bottom")])],"isStart":false});
            fillet(context, id + "F15", {"entities" : qUnion([Q0]), "radius" : 2 * mm, "tangentPropagation" : true, "allowEdgeOverflow" : false});
        }
        {
            var Q0;
            {var subQ0=sQuery(id+"F0.wireOp",EDGE,"E22.filletArc");var subQ1=sQuery(id+"F0.wireOp",EDGE,"E7");var subQ2=sQuery(id+"F0.wireOp",EDGE,"E6");var subQ3=sQuery(id+"F0.wireOp",EDGE,"E5");var subQ4=sQuery(id+"F0.wireOp",EDGE,"E4");var subQ5=sQuery(id+"F0.wireOp",EDGE,"E1.bottom");var subQ6=sQuery(id+"F0.wireOp",EDGE,"E21.filletArc");var subQ7=sQuery(id+"F0.wireOp",EDGE,"E1.top");var subQ8=sQuery(id+"F0.wireOp",EDGE,"E1.left");var subQ9=sQuery(id+"F0.wireOp",EDGE,"E1.right");var subQ10=sQuery(id+"F0.wireOp",EDGE,"E23.filletArc");var subQ11=sQuery(id+"F0.wireOp",EDGE,"E24.filletArc");Q0=makeQuery(id+"F2.boolean.opBoolean","SPLIT",FACE,{"disambiguationData":[TD([makeQuery(id+"F1.opExtrude","SWEPT_FACE",FACE,{"disambiguationData":[OSD([subQ5])]})])],"derivedFrom":makeQuery(id+"F1.opExtrude","CAP_FACE",FACE,{"disambiguationData":[OSD([subQ5,subQ7,subQ8,subQ9,subQ4,subQ3,subQ2,subQ1,subQ6,subQ0,subQ10,subQ11])],"isStart":true})});}
            var sketch = newSketch(context, id + "F16", { "sketchPlane" : qUnion([Q0])});
            skLineSegment(sketch, "E79", {"start": v(-33, 74.25) * mm, "end": v(-15, 92.25) * mm});
            skLineSegment(sketch, "E80", {"start": v(-15, 92.25) * mm, "end": v(-15, 104.25) * mm});
            skArc(sketch, "E81", {"start": v(15, 104.25) * mm, "mid": v(0, 119.25) * mm, "end": v(-15, 104.25) * mm});
            skLineSegment(sketch, "E82", {"start": v(15, 104.25) * mm, "end": v(15, 92.25) * mm});
            skLineSegment(sketch, "E83", {"start": v(15, 92.25) * mm, "end": v(33, 74.25) * mm});
            skCircle(sketch, "E84", {"center": v(0, 104.25) * mm, "radius": 6 * mm});
            skPoint(sketch, "E85", {"position": v(0, 74.25) * mm});
            skLineSegment(sketch, "E86", {"start": v(0, 104.25) * mm, "end": v(0, 74.25) * mm, "construction": true});
            skPoint(sketch, "E87.end.orphan", {"position": v(0, -74.25) * mm});
            skLineSegment(sketch, "E88", {"start": v(-74.25, 0) * mm, "end": v(74.25, 0) * mm, "construction": true});
            skLineSegment(sketch, "E89.MirrorCS", {"start": v(-33, -74.25) * mm, "end": v(-15, -92.25) * mm});
            skLineSegment(sketch, "E90.MirrorCS", {"start": v(-15, -92.25) * mm, "end": v(-15, -104.25) * mm});
            skLineSegment(sketch, "E91.MirrorCS", {"start": v(0, -104.25) * mm, "end": v(0, -74.25) * mm, "construction": true});
            skLineSegment(sketch, "E92.MirrorCS", {"start": v(15, -92.25) * mm, "end": v(33, -74.25) * mm});
            skLineSegment(sketch, "E93.MirrorCS", {"start": v(15, -104.25) * mm, "end": v(15, -92.25) * mm});
            skArc(sketch, "E94.MirrorCS", {"start": v(15, -104.25) * mm, "mid": v(0, -119.25) * mm, "end": v(-15, -104.25) * mm});
            skCircle(sketch, "E95.MirrorC", {"center": v(0, -104.25) * mm, "radius": 6 * mm});
            skSolve(sketch);
        }
        {
            var Q0;
            {var subQ1=sQuery(id+"F16.wireOp",EDGE,"E89.MirrorCS");Q0=makeQuery(id+"F16.imprint","IMPRINT",FACE,{"disambiguationData":[TD([[makeQuery(id+"F16.imprint","IMPRINT",EDGE,{"derivedFrom":subQ1}),1.0]])]});}
            var Q1;
            Q1=makeQuery(id+"F16.imprint","IMPRINT",FACE,{"disambiguationData":[TD([[makeQuery(id+"F16.imprint","IMPRINT",EDGE,{"derivedFrom":makeQuery(id+"F1.opExtrude","CAP_EDGE",EDGE,{"disambiguationData":[OSD([sQuery(id+"F0.wireOp",EDGE,"E1.left")])],"isStart":true})}),-1.0]])]});
            var Q2;
            {var subQ0=sQuery(id+"F16.wireOp",EDGE,"E79");Q2=makeQuery(id+"F16.imprint","IMPRINT",FACE,{"disambiguationData":[TD([[makeQuery(id+"F16.imprint","IMPRINT",EDGE,{"derivedFrom":subQ0}),-1.0]])]});}
            var Q3;
            Q3=makeQuery(id+"F2.opExtrude","CAP_FACE",FACE,{"disambiguationData":[OSD([sQuery(id+"F0.wireOp",EDGE,"E12"),sQuery(id+"F0.wireOp",EDGE,"E13"),sQuery(id+"F0.wireOp",EDGE,"E14"),sQuery(id+"F0.wireOp",EDGE,"E15"),sQuery(id+"F0.wireOp",EDGE,"E17.filletArc"),sQuery(id+"F0.wireOp",EDGE,"E18.filletArc"),sQuery(id+"F0.wireOp",EDGE,"E19.filletArc"),sQuery(id+"F0.wireOp",EDGE,"E20.filletArc"),sQuery(id+"F0.wireOp",EDGE,"E25.0"),sQuery(id+"F0.wireOp",EDGE,"E25.1"),sQuery(id+"F0.wireOp",EDGE,"E25.2"),sQuery(id+"F0.wireOp",EDGE,"E25.3"),sQuery(id+"F0.wireOp",EDGE,"E25.4"),sQuery(id+"F0.wireOp",EDGE,"E25.5"),sQuery(id+"F0.wireOp",EDGE,"E25.6"),sQuery(id+"F0.wireOp",EDGE,"E25.7")])],"isStart":false});
            extrude(context, id + "F17", {"entities" : qUnion([Q0, Q1, Q2]), "endBound" : BoundingType.UP_TO_SURFACE, "endBoundEntityFace" : qUnion([Q3]), "depth" : 25 * mm});
        }
    });
